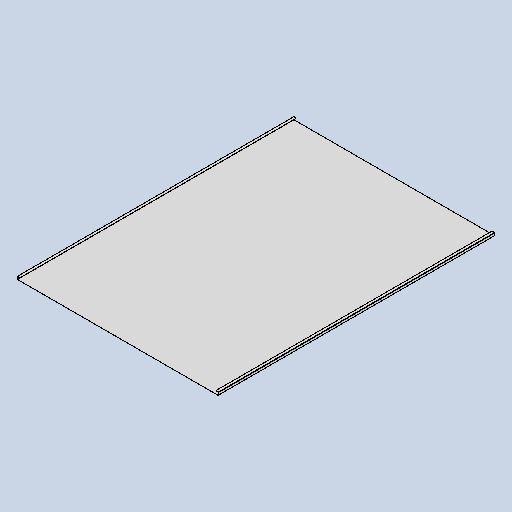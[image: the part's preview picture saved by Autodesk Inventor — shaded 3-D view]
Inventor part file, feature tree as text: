
AUTODESK INVENTOR PART (.ipt)
format: ipt  version: 2025 (Build 290162010, 162A)  size: 194,560 bytes
history: native  units: mm
features: sheet_metal_op x13, other x6, sketch x5, chamfer x1
ambient origin geometry x8: Origin, YZ Plane, XZ Plane, XY Plane, X Axis, Y Axis, Z Axis, Center Point
bodies: Body1 (feature_tree)
feature tree (25):
  sheet_metal_op  "Face1"
  sheet_metal_op  "Flange2"
  sheet_metal_op  "Flange3"
  sheet_metal_op  "Flange4"
  sheet_metal_op  "Flange5"
  chamfer  "Corner Round1"
  sketch  "Sketch6"  dims[d12=23.212879mm]
  other  "Plate2"
  sketch  "Sketch11"  dims[d52=713.4mm]
  other  "Plate4"
  sheet_metal_op  "Bend3"
  sheet_metal_op  "Corner3"
  sketch  "Sketch12"  dims[d53=980.0mm]
  other  "Plate5"
  sheet_metal_op  "Bend4"
  sheet_metal_op  "Corner4"
  sketch  "Sketch13"  dims[d54=0.5mm]
  other  "Plate6"
  sheet_metal_op  "Bend5"
  sheet_metal_op  "Corner5"
  sketch  "Sketch14"  dims[d84=0.5mm d85=0.25mm d86=1.0mm d87=0.5mm d88=10.0mm d89=90.0deg d90=0.5mm d91=2.0mm d92=0.5mm d93=0.5mm d94=0.5mm d95=0.25mm d96=1.0mm d97=0.5mm d98=10.0mm d99=90.0deg d100=0.5mm d101=2.0mm d102=0.5mm d103=0.5mm d104=0.5mm d105=0.25mm d106=1.0mm d107=0.5mm d108=10.0mm d109=90.0deg d110=0.5mm d111=2.0mm d112=0.5mm d113=0.5mm d114=0.5mm d115=0.25mm d116=1.0mm d117=0.5mm d118=10.0mm d119=90.0deg d120=0.5mm d121=2.0mm d122=0.5mm d123=0.5mm d124=4.0mm]
  other  "Plate7"
  sheet_metal_op  "Bend6"
  sheet_metal_op  "Corner6"
  other  "Definition1"
